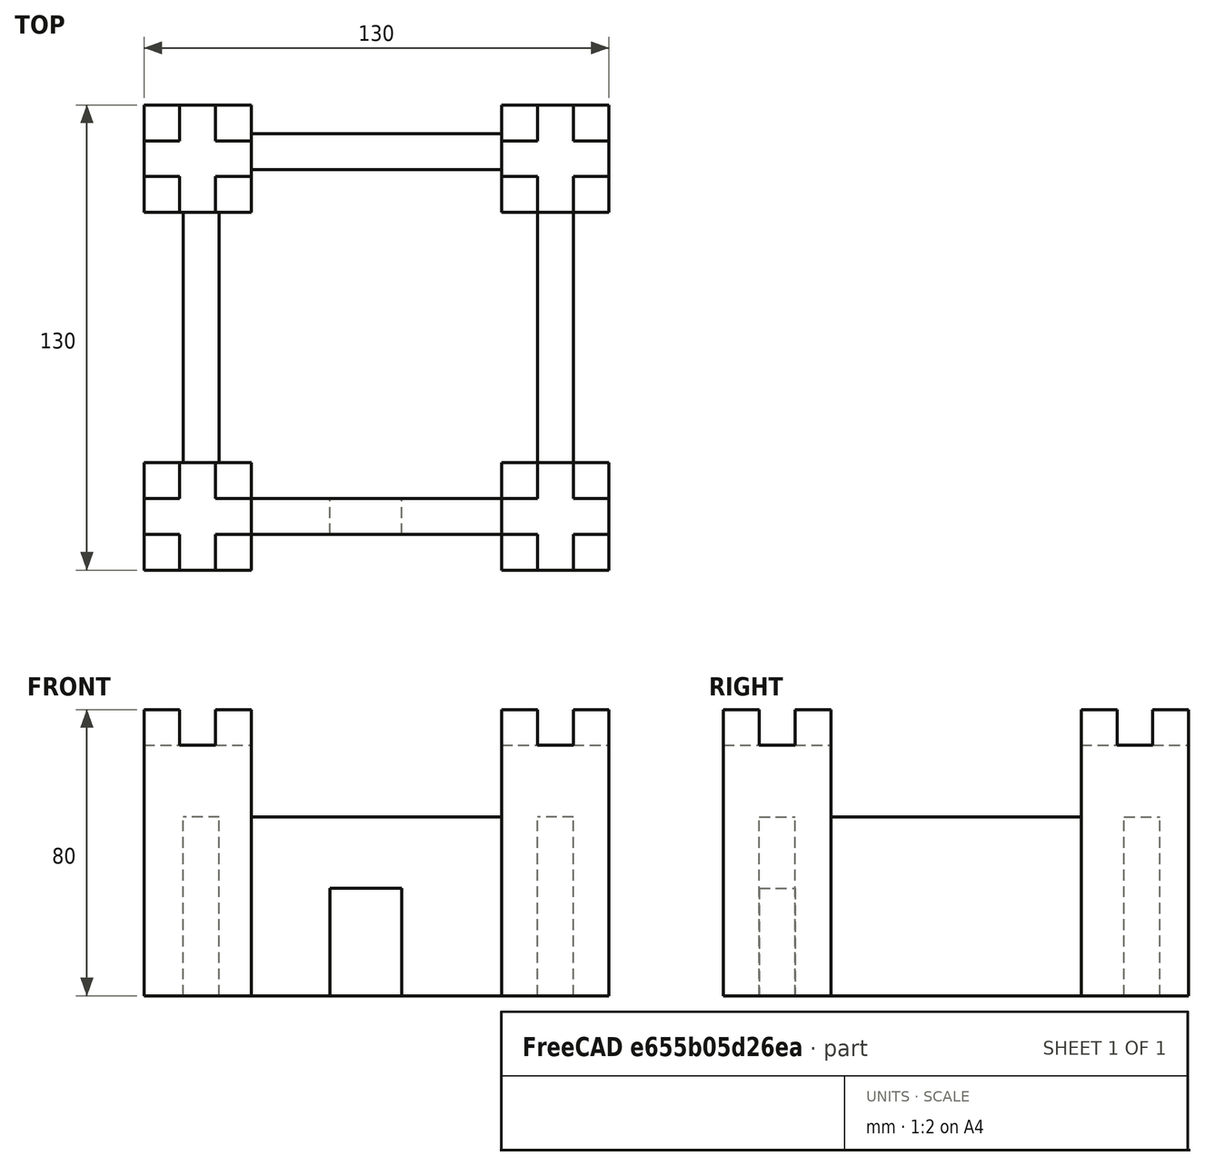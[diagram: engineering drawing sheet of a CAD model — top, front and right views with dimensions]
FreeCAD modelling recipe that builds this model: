
FCSTD DOCUMENT  (FreeCAD 0.17R12412 (Git))
Label: 02-castle
License: All rights reserved
LicenseURL: http://en.wikipedia.org/wiki/All_rights_reserved
objects: Part::Box×10, Part::MultiFuse×5, Part::Cut×1
note: 16 computed .brp shape members not serialized (recipe doc carries the construction recipe); baked Part::Feature solids carry a one-line shape summary decoded from their .brp

FEATURE [Part::Box] Box  label="Cube"
  AttacherType = Attacher::AttachEngine3D
  Height = 70
  Length = 30
  Width = 30
FEATURE [Part::Box] Box001  label="Cube001"
  AttacherType = Attacher::AttachEngine3D
  Height = 10
  Length = 10
  Placement = pos=(0,0,70) rot=(0,0,1;0rad)
  Width = 10
FEATURE [Part::Box] Box002  label="Cube002"
  AttacherType = Attacher::AttachEngine3D
  Height = 10
  Length = 10
  Placement = pos=(20,0,70) rot=(0,0,1;0rad)
  Width = 10
FEATURE [Part::Box] Box003  label="Cube003"
  AttacherType = Attacher::AttachEngine3D
  Height = 10
  Length = 10
  Placement = pos=(0,20,70) rot=(0,0,1;0rad)
  Width = 10
FEATURE [Part::Box] Box004  label="Cube004"
  AttacherType = Attacher::AttachEngine3D
  Height = 10
  Length = 10
  Placement = pos=(20,20,70) rot=(0,0,1;0rad)
  Width = 10
FEATURE [Part::MultiFuse] Fusion  label="Tower-1"
  Shapes = -> [Box,Box001,Box004,Box003,Box002]
FEATURE [Part::MultiFuse] Fusion001  label="Tower-3"
  Placement = pos=(100,0,0) rot=(0,0,1;0rad)
  Shapes = -> [Box,Box001,Box004,Box003,Box002]
FEATURE [Part::MultiFuse] Fusion002  label="Tower-2"
  Placement = pos=(0,100,0) rot=(0,0,1;0rad)
  Shapes = -> [Box,Box001,Box004,Box003,Box002]
FEATURE [Part::MultiFuse] Fusion003  label="Tower-4"
  Placement = pos=(100,100,0) rot=(0,0,1;0rad)
  Shapes = -> [Box,Box001,Box004,Box003,Box002]
FEATURE [Part::Box] Box005  label="front-wall"
  AttacherType = Attacher::AttachEngine3D
  Height = 50
  Length = 70
  Placement = pos=(30,10,0) rot=(0,0,1;0rad)
  Width = 10
FEATURE [Part::Box] Box006  label="back-wall"
  AttacherType = Attacher::AttachEngine3D
  Height = 50
  Length = 70
  Placement = pos=(30,112,0) rot=(0,0,1;0rad)
  Width = 10
FEATURE [Part::Box] Box007  label="left-wall"
  AttacherType = Attacher::AttachEngine3D
  Height = 50
  Length = 70
  Placement = pos=(21,30,0) rot=(0,0,1;1.5708rad)
  Width = 10
FEATURE [Part::Box] Box008  label="right-wall"
  AttacherType = Attacher::AttachEngine3D
  Height = 50
  Length = 70
  Placement = pos=(120,30,0) rot=(0,0,1;1.5708rad)
  Width = 10
FEATURE [Part::MultiFuse] Fusion004  label="Castle-body"
  Shapes = -> [Fusion,Box008,Box005,Fusion002,Box007,Fusion001,Box006,Fusion003]
FEATURE [Part::Box] Box009  label="main_door"
  AttacherType = Attacher::AttachEngine3D
  Height = 30
  Length = 20
  Placement = pos=(52,0,0) rot=(0,0,1;0rad)
  Width = 30
FEATURE [Part::Cut] Cut  label="Castle"
  Base = -> Fusion004
  Tool = -> Box009
